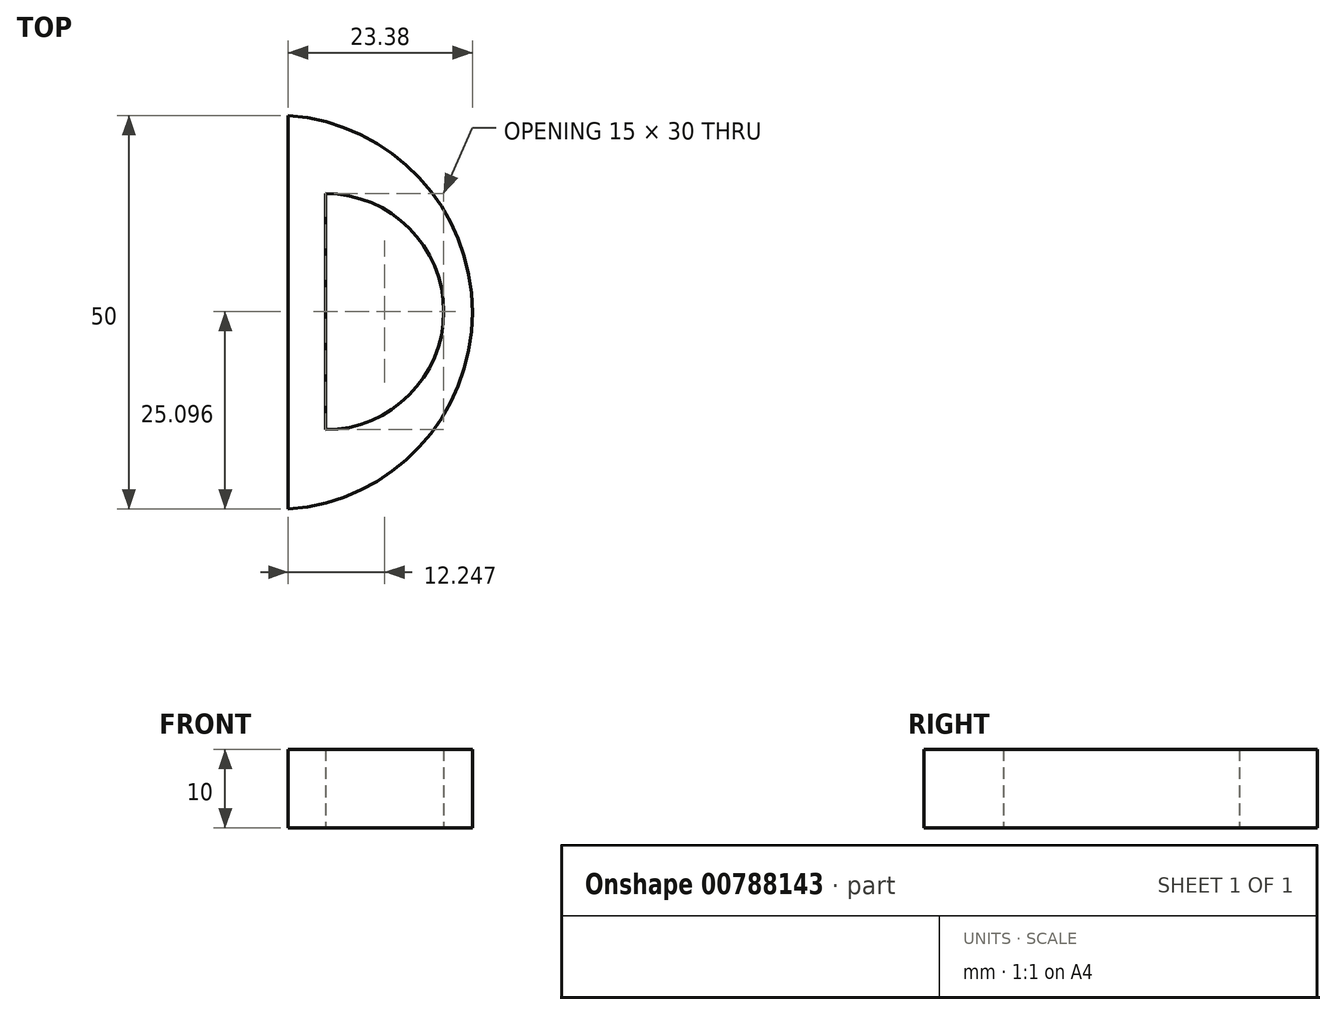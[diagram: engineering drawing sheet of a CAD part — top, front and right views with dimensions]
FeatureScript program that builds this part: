
annotation { "Feature Type Name" : "Feature", "Feature Type Description" : "" }
export const myFeature = defineFeature(function(context is Context, id is Id, definition is map)
    precondition{}
    {
        {
            var Q0;
            Q0=qCreatedBy(makeId("Top.planeOp"),FACE);
            var sketch = newSketch(context, id + "F0", { "sketchPlane" : qUnion([Q0])});
            skLineSegment(sketch, "E0", {"start": v(-15.24, 31.4) * mm, "end": v(-15.24, -18.6) * mm});
            skArc(sketch, "E1", {"start": v(-15.24, -18.6) * mm, "mid": v(8.14, 6.4) * mm, "end": v(-15.24, 31.4) * mm});
            skLineSegment(sketch, "E2", {"start": v(-10.5, 21.5) * mm, "end": v(-10.5, -8.5) * mm});
            skArc(sketch, "E3", {"start": v(-10.5, -8.5) * mm, "mid": v(4.5, 6.5) * mm, "end": v(-10.5, 21.5) * mm});
            skSolve(sketch);
        }
        {
            var Q0;
            Q0=makeQuery(id+"F0.imprint","IMPRINT",FACE,{"disambiguationData":[TD([[makeQuery(id+"F0.imprint","IMPRINT",EDGE,{"derivedFrom":sQuery(id+"F0.wireOp",EDGE,"E0")}),1.0]])]});
            extrude(context, id + "F1", {"entities" : qUnion([Q0]), "depth" : 10 * mm, "offsetDistance" : 25 * mm});
        }
    });
